# Revit family: Operable-Walls_Modernfold_Acousti-Clear_Automatic_Paired-Panels_Pivot-Panel-Egress
name_source: partatom
category: Specialty Equipment
units: mm (PartAtom-declared; Revit-internal decimal feet)

## family parameters
Always vertical = Yes
Classification Number = 23.25.40.17.14
Cut with Voids When Loaded = No
Enable Cutting in Views = No
Maintain Annotation Orientation = No
Part Type = Normal
Room Calculation Point = No
Round Connector Dimension = Use Diameter
Shared = No
Work Plane-Based = No

## types (2) — shared parameters
Bottom Seal Height = 0' - 1"
Clearance Right = 3' - 10"
Default Elevation = 0' - 0"
Manufacturer = Modernfold
Model = Acousti-Seal® Legacy® & Premier®
Panel Material = Wall finish - Modernfold - Anodized aluminium
Panel Thickness = 0' - 4"
Seal Material = Seal Finish - Modernfold - Black
Seal Width = 0' - 2 1/2"
Track Material = Track Color - Modernfold - White
Track Trim = 0' - 1"
Trim Material = Wall finish - Modernfold - Anodized aluminium
URL = https://www.modernfold.com
zWallJambVis = Yes

## per-type parameters (varying)
| type | Description |
| Lever Handle | Acousti-Clear - Pivot Panel - Paired Panels - Lever Handle |
| Rail Handle | Acousti-Clear - Pivot Panel - Paired Panels - Rail Handle |

type visibility flags: 2 boolean params named "<type name>" — each type sets only its own to Yes (folded from table)

## geometry (parser evidence)
native form markers: Sweep x22
no freeform markers — native parametric forms only
